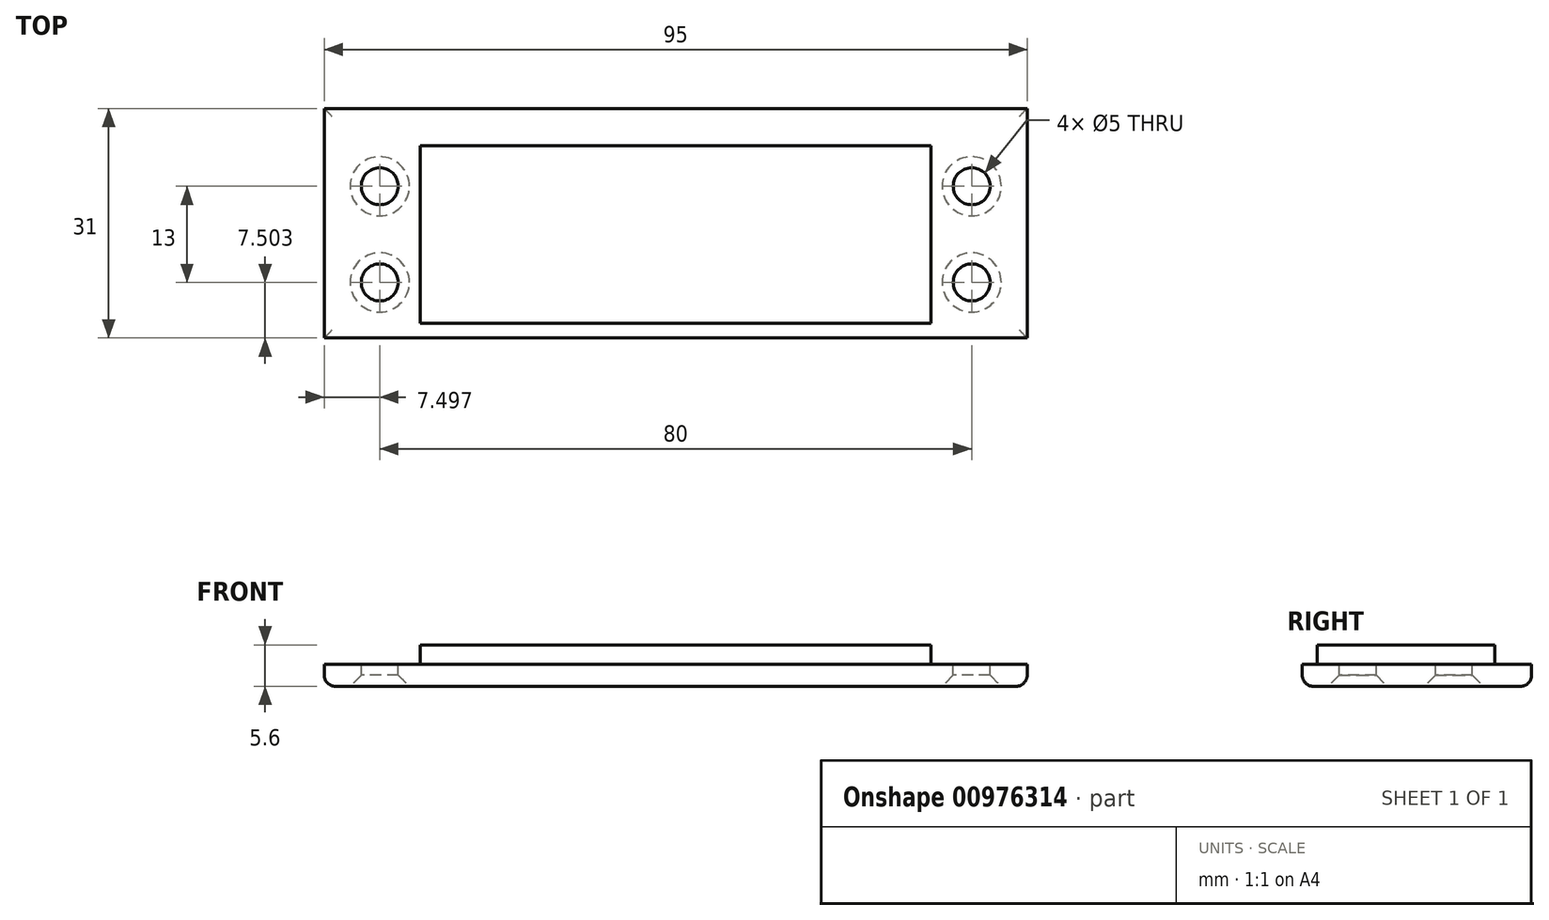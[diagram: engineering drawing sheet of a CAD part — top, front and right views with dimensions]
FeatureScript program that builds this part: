
annotation { "Feature Type Name" : "Feature", "Feature Type Description" : "" }
export const myFeature = defineFeature(function(context is Context, id is Id, definition is map)
    precondition{}
    {
        {
            var Q0;
            Q0=qCreatedBy(makeId("Top.planeOp"),FACE);
            var sketch = newSketch(context, id + "F0", { "sketchPlane" : qUnion([Q0])});
            skLineSegment(sketch, "E0.bottom", {"start": v(-40.05, 0.14) * mm, "end": v(54.95, 0.14) * mm});
            skLineSegment(sketch, "E0.top", {"start": v(-40.05, -30.86) * mm, "end": v(54.95, -30.86) * mm});
            skLineSegment(sketch, "E0.left", {"start": v(-40.05, 0.14) * mm, "end": v(-40.05, -30.86) * mm});
            skLineSegment(sketch, "E0.right", {"start": v(54.95, 0.14) * mm, "end": v(54.95, -30.86) * mm});
            skLineSegment(sketch, "E1.bottom", {"start": v(-27.05, -4.86) * mm, "end": v(41.95, -4.86) * mm});
            skLineSegment(sketch, "E1.top", {"start": v(-27.05, -28.86) * mm, "end": v(41.95, -28.86) * mm});
            skLineSegment(sketch, "E1.left", {"start": v(-27.05, -4.86) * mm, "end": v(-27.05, -28.86) * mm});
            skLineSegment(sketch, "E1.right", {"start": v(41.95, -4.86) * mm, "end": v(41.95, -28.86) * mm});
            skSolve(sketch);
        }
        {
            var Q0;
            Q0=makeQuery(id+"F0.imprint","IMPRINT",FACE,{"disambiguationData":[TD([[makeQuery(id+"F0.imprint","IMPRINT",EDGE,{"derivedFrom":sQuery(id+"F0.wireOp",EDGE,"E0.bottom")}),-1.0]])]});
            extrude(context, id + "F1", {"entities" : qUnion([Q0]), "depth" : 3 * mm, "offsetDistance" : 25 * mm});
        }
        {
            var Q0;
            Q0=makeQuery(id+"F0.imprint","IMPRINT",FACE,{"disambiguationData":[TD([[makeQuery(id+"F0.imprint","IMPRINT",EDGE,{"derivedFrom":sQuery(id+"F0.wireOp",EDGE,"E1.bottom")}),-1.0]])]});
            extrude(context, id + "F2", {"entities" : qUnion([Q0]), "operationType" : NewBodyOperationType.ADD, "depth" : 5.6 * mm, "offsetDistance" : 25 * mm});
        }
        {
            var Q0;
            Q0=makeQuery(id+"F1.opExtrude","CAP_EDGE",EDGE,{"disambiguationData":[OSD([sQuery(id+"F0.wireOp",EDGE,"E0.left")])],"isStart":true});
            var Q1;
            Q1=makeQuery(id+"F1.opExtrude","CAP_EDGE",EDGE,{"disambiguationData":[OSD([sQuery(id+"F0.wireOp",EDGE,"E0.bottom")])],"isStart":true});
            var Q2;
            Q2=makeQuery(id+"F1.opExtrude","CAP_EDGE",EDGE,{"disambiguationData":[OSD([sQuery(id+"F0.wireOp",EDGE,"E0.top")])],"isStart":true});
            var Q3;
            Q3=makeQuery(id+"F1.opExtrude","CAP_EDGE",EDGE,{"disambiguationData":[OSD([sQuery(id+"F0.wireOp",EDGE,"E0.right")])],"isStart":true});
            fillet(context, id + "F3", {"entities" : qUnion([Q0, Q1, Q2, Q3]), "radius" : 1.5 * mm, "tangentPropagation" : true, "allowEdgeOverflow" : false});
        }
        {
            var Q0;
            Q0=makeQuery(id+"F2.opExtrude","CAP_FACE",FACE,{"disambiguationData":[OSD([sQuery(id+"F0.wireOp",EDGE,"E1.bottom"),sQuery(id+"F0.wireOp",EDGE,"E1.top"),sQuery(id+"F0.wireOp",EDGE,"E1.left"),sQuery(id+"F0.wireOp",EDGE,"E1.right")])],"isStart":false});
            var sketch = newSketch(context, id + "F4", { "sketchPlane" : qUnion([Q0])});
            skCircle(sketch, "E2", {"center": v(-32.55, -10.36) * mm, "radius": 2.5 * mm});
            skCircle(sketch, "E3", {"center": v(-32.55, -23.36) * mm, "radius": 2.5 * mm});
            skCircle(sketch, "E4", {"center": v(47.45, -23.36) * mm, "radius": 2.5 * mm});
            skCircle(sketch, "E5", {"center": v(47.45, -10.36) * mm, "radius": 2.5 * mm});
            skSolve(sketch);
        }
        {
            var Q0;
            Q0 = qSketchRegion(id + "F4", true);
            extrude(context, id + "F5", {"entities" : qUnion([Q0]), "operationType" : NewBodyOperationType.REMOVE, "oppositeDirection" : true, "depth" : 25 * mm, "offsetDistance" : 25 * mm});
        }
        {
            var Q0;
            {var subQ0=sQuery(id+"F0.wireOp",EDGE,"E1.right");var subQ1=sQuery(id+"F0.wireOp",EDGE,"E1.left");var subQ2=sQuery(id+"F0.wireOp",EDGE,"E1.top");var subQ3=sQuery(id+"F0.wireOp",EDGE,"E1.bottom");Q0=makeQuery(id+"F5.boolean.opBoolean","INTERSECT",EDGE,{"derivedFrom":[makeQuery(id+"F2.boolean.opBoolean","MERGE",FACE,{"derivedFrom":[makeQuery(id+"F1.opExtrude","CAP_FACE",FACE,{"disambiguationData":[OSD([sQuery(id+"F0.wireOp",EDGE,"E0.bottom"),sQuery(id+"F0.wireOp",EDGE,"E0.top"),sQuery(id+"F0.wireOp",EDGE,"E0.left"),sQuery(id+"F0.wireOp",EDGE,"E0.right"),subQ3,subQ2,subQ1,subQ0])],"isStart":true}),makeQuery(id+"F2.opExtrude","CAP_FACE",FACE,{"disambiguationData":[OSD([subQ3,subQ2,subQ1,subQ0])],"isStart":true})]}),makeQuery(id+"F5.opExtrude","SWEPT_FACE",FACE,{"disambiguationData":[OSD([sQuery(id+"F4.wireOp",EDGE,"E3")])]})]});}
            var Q1;
            {var subQ0=sQuery(id+"F0.wireOp",EDGE,"E1.right");var subQ1=sQuery(id+"F0.wireOp",EDGE,"E1.left");var subQ2=sQuery(id+"F0.wireOp",EDGE,"E1.top");var subQ3=sQuery(id+"F0.wireOp",EDGE,"E1.bottom");Q1=makeQuery(id+"F5.boolean.opBoolean","INTERSECT",EDGE,{"derivedFrom":[makeQuery(id+"F2.boolean.opBoolean","MERGE",FACE,{"derivedFrom":[makeQuery(id+"F1.opExtrude","CAP_FACE",FACE,{"disambiguationData":[OSD([sQuery(id+"F0.wireOp",EDGE,"E0.bottom"),sQuery(id+"F0.wireOp",EDGE,"E0.top"),sQuery(id+"F0.wireOp",EDGE,"E0.left"),sQuery(id+"F0.wireOp",EDGE,"E0.right"),subQ3,subQ2,subQ1,subQ0])],"isStart":true}),makeQuery(id+"F2.opExtrude","CAP_FACE",FACE,{"disambiguationData":[OSD([subQ3,subQ2,subQ1,subQ0])],"isStart":true})]}),makeQuery(id+"F5.opExtrude","SWEPT_FACE",FACE,{"disambiguationData":[OSD([sQuery(id+"F4.wireOp",EDGE,"E2")])]})]});}
            var Q2;
            {var subQ0=sQuery(id+"F0.wireOp",EDGE,"E1.right");var subQ1=sQuery(id+"F0.wireOp",EDGE,"E1.left");var subQ2=sQuery(id+"F0.wireOp",EDGE,"E1.top");var subQ3=sQuery(id+"F0.wireOp",EDGE,"E1.bottom");Q2=makeQuery(id+"F5.boolean.opBoolean","INTERSECT",EDGE,{"derivedFrom":[makeQuery(id+"F2.boolean.opBoolean","MERGE",FACE,{"derivedFrom":[makeQuery(id+"F1.opExtrude","CAP_FACE",FACE,{"disambiguationData":[OSD([sQuery(id+"F0.wireOp",EDGE,"E0.bottom"),sQuery(id+"F0.wireOp",EDGE,"E0.top"),sQuery(id+"F0.wireOp",EDGE,"E0.left"),sQuery(id+"F0.wireOp",EDGE,"E0.right"),subQ3,subQ2,subQ1,subQ0])],"isStart":true}),makeQuery(id+"F2.opExtrude","CAP_FACE",FACE,{"disambiguationData":[OSD([subQ3,subQ2,subQ1,subQ0])],"isStart":true})]}),makeQuery(id+"F5.opExtrude","SWEPT_FACE",FACE,{"disambiguationData":[OSD([sQuery(id+"F4.wireOp",EDGE,"E5")])]})]});}
            var Q3;
            {var subQ0=sQuery(id+"F0.wireOp",EDGE,"E1.right");var subQ1=sQuery(id+"F0.wireOp",EDGE,"E1.left");var subQ2=sQuery(id+"F0.wireOp",EDGE,"E1.top");var subQ3=sQuery(id+"F0.wireOp",EDGE,"E1.bottom");Q3=makeQuery(id+"F5.boolean.opBoolean","INTERSECT",EDGE,{"derivedFrom":[makeQuery(id+"F2.boolean.opBoolean","MERGE",FACE,{"derivedFrom":[makeQuery(id+"F1.opExtrude","CAP_FACE",FACE,{"disambiguationData":[OSD([sQuery(id+"F0.wireOp",EDGE,"E0.bottom"),sQuery(id+"F0.wireOp",EDGE,"E0.top"),sQuery(id+"F0.wireOp",EDGE,"E0.left"),sQuery(id+"F0.wireOp",EDGE,"E0.right"),subQ3,subQ2,subQ1,subQ0])],"isStart":true}),makeQuery(id+"F2.opExtrude","CAP_FACE",FACE,{"disambiguationData":[OSD([subQ3,subQ2,subQ1,subQ0])],"isStart":true})]}),makeQuery(id+"F5.opExtrude","SWEPT_FACE",FACE,{"disambiguationData":[OSD([sQuery(id+"F4.wireOp",EDGE,"E4")])]})]});}
            chamfer(context, id + "F6", {"entities" : qUnion([Q0, Q1, Q2, Q3]), "width" : 1.5 * mm, "tangentPropagation" : true});
        }
    });
